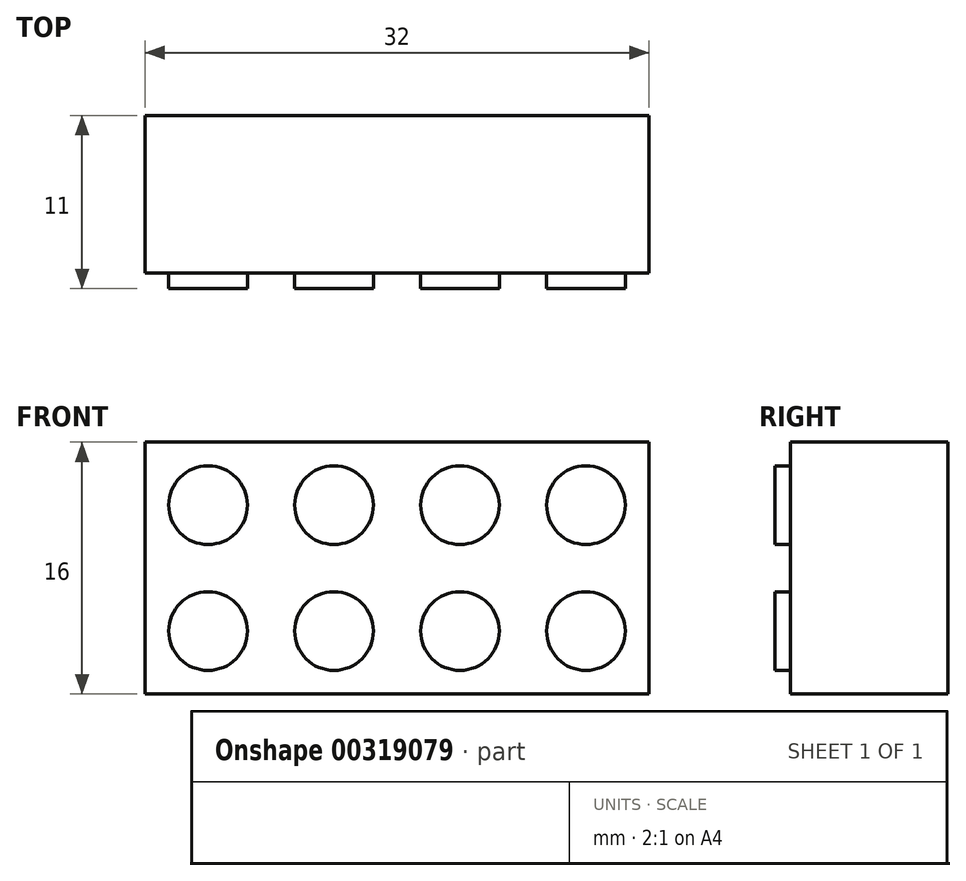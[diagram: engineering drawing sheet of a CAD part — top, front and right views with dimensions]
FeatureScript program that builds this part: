
annotation { "Feature Type Name" : "Feature", "Feature Type Description" : "" }
export const myFeature = defineFeature(function(context is Context, id is Id, definition is map)
    precondition{}
    {
        {
            var Q0;
            Q0=qCreatedBy(makeId("Front.planeOp"),FACE);
            var sketch = newSketch(context, id + "F0", { "sketchPlane" : qUnion([Q0])});
            skLineSegment(sketch, "E0.bottom", {"start": v(-16, -8) * mm, "end": v(16, -8) * mm});
            skLineSegment(sketch, "E0.top", {"start": v(-16, 8) * mm, "end": v(16, 8) * mm});
            skLineSegment(sketch, "E0.left", {"start": v(-16, -8) * mm, "end": v(-16, 8) * mm});
            skLineSegment(sketch, "E0.right", {"start": v(16, -8) * mm, "end": v(16, 8) * mm});
            skPoint(sketch, "E0.middle", {"position": v(0, 0) * mm});
            skCircle(sketch, "E1", {"center": v(-12, 4) * mm, "radius": 2.5 * mm});
            skCircle(sketch, "E2", {"center": v(-12, -4) * mm, "radius": 2.5 * mm});
            skCircle(sketch, "E3", {"center": v(-4, -4) * mm, "radius": 2.5 * mm});
            skCircle(sketch, "E4", {"center": v(4, -4) * mm, "radius": 2.5 * mm});
            skCircle(sketch, "E5", {"center": v(12, -4) * mm, "radius": 2.5 * mm});
            skCircle(sketch, "E6", {"center": v(-4, 4) * mm, "radius": 2.5 * mm});
            skCircle(sketch, "E7", {"center": v(4, 4) * mm, "radius": 2.5 * mm});
            skCircle(sketch, "E8", {"center": v(12, 4) * mm, "radius": 2.5 * mm});
            skSolve(sketch);
        }
        {
            var Q0;
            Q0=makeQuery(id+"F0.imprint","IMPRINT",FACE,{"disambiguationData":[TD([[makeQuery(id+"F0.imprint","IMPRINT",EDGE,{"derivedFrom":sQuery(id+"F0.wireOp",EDGE,"E0.bottom")}),1.0]])]});
            extrude(context, id + "F1", {"entities" : qUnion([Q0]), "oppositeDirection" : true, "depth" : 10 * mm});
        }
        {
            var Q0;
            Q0=makeQuery(id+"F1.opExtrude","CAP_FACE",FACE,{"disambiguationData":[OSD([sQuery(id+"F0.wireOp",EDGE,"E0.bottom"),sQuery(id+"F0.wireOp",EDGE,"E0.top"),sQuery(id+"F0.wireOp",EDGE,"E0.left"),sQuery(id+"F0.wireOp",EDGE,"E0.right"),sQuery(id+"F0.wireOp",EDGE,"E1"),sQuery(id+"F0.wireOp",EDGE,"E2"),sQuery(id+"F0.wireOp",EDGE,"E3"),sQuery(id+"F0.wireOp",EDGE,"E4"),sQuery(id+"F0.wireOp",EDGE,"E5"),sQuery(id+"F0.wireOp",EDGE,"E6"),sQuery(id+"F0.wireOp",EDGE,"E7"),sQuery(id+"F0.wireOp",EDGE,"E8")])],"isStart":false});
            var sketch = newSketch(context, id + "F2", { "sketchPlane" : qUnion([Q0])});
            skSolve(sketch);
        }
        {
            var Q0;
            Q0 = qSketchRegion(id + "F2", true);
            var Q1;
            Q1=makeQuery(id+"F2.imprint","IMPRINT",FACE,{"disambiguationData":[TD([[makeQuery(id+"F2.imprint","IMPRINT",EDGE,{"derivedFrom":makeQuery(id+"F1.opExtrude","CAP_EDGE",EDGE,{"disambiguationData":[OSD([sQuery(id+"F0.wireOp",EDGE,"E2")])],"isStart":false})}),-1.0]])]});
            var Q2;
            Q2=makeQuery(id+"F2.imprint","IMPRINT",FACE,{"disambiguationData":[TD([[makeQuery(id+"F2.imprint","IMPRINT",EDGE,{"derivedFrom":makeQuery(id+"F1.opExtrude","CAP_EDGE",EDGE,{"disambiguationData":[OSD([sQuery(id+"F0.wireOp",EDGE,"E1")])],"isStart":false})}),-1.0]])]});
            var Q3;
            Q3=makeQuery(id+"F2.imprint","IMPRINT",FACE,{"disambiguationData":[TD([[makeQuery(id+"F2.imprint","IMPRINT",EDGE,{"derivedFrom":makeQuery(id+"F1.opExtrude","CAP_EDGE",EDGE,{"disambiguationData":[OSD([sQuery(id+"F0.wireOp",EDGE,"E6")])],"isStart":false})}),-1.0]])]});
            var Q4;
            Q4=makeQuery(id+"F2.imprint","IMPRINT",FACE,{"disambiguationData":[TD([[makeQuery(id+"F2.imprint","IMPRINT",EDGE,{"derivedFrom":makeQuery(id+"F1.opExtrude","CAP_EDGE",EDGE,{"disambiguationData":[OSD([sQuery(id+"F0.wireOp",EDGE,"E3")])],"isStart":false})}),-1.0]])]});
            var Q5;
            Q5=makeQuery(id+"F2.imprint","IMPRINT",FACE,{"disambiguationData":[TD([[makeQuery(id+"F2.imprint","IMPRINT",EDGE,{"derivedFrom":makeQuery(id+"F1.opExtrude","CAP_EDGE",EDGE,{"disambiguationData":[OSD([sQuery(id+"F0.wireOp",EDGE,"E4")])],"isStart":false})}),-1.0]])]});
            var Q6;
            Q6=makeQuery(id+"F2.imprint","IMPRINT",FACE,{"disambiguationData":[TD([[makeQuery(id+"F2.imprint","IMPRINT",EDGE,{"derivedFrom":makeQuery(id+"F1.opExtrude","CAP_EDGE",EDGE,{"disambiguationData":[OSD([sQuery(id+"F0.wireOp",EDGE,"E7")])],"isStart":false})}),-1.0]])]});
            var Q7;
            Q7=makeQuery(id+"F2.imprint","IMPRINT",FACE,{"disambiguationData":[TD([[makeQuery(id+"F2.imprint","IMPRINT",EDGE,{"derivedFrom":makeQuery(id+"F1.opExtrude","CAP_EDGE",EDGE,{"disambiguationData":[OSD([sQuery(id+"F0.wireOp",EDGE,"E5")])],"isStart":false})}),-1.0]])]});
            var Q8;
            Q8=makeQuery(id+"F2.imprint","IMPRINT",FACE,{"disambiguationData":[TD([[makeQuery(id+"F2.imprint","IMPRINT",EDGE,{"derivedFrom":makeQuery(id+"F1.opExtrude","CAP_EDGE",EDGE,{"disambiguationData":[OSD([sQuery(id+"F0.wireOp",EDGE,"E8")])],"isStart":false})}),-1.0]])]});
            extrude(context, id + "F3", {"entities" : qUnion([Q0, Q1, Q2, Q3, Q4, Q5, Q6, Q7, Q8]), "operationType" : NewBodyOperationType.ADD, "oppositeDirection" : true, "depth" : 11 * mm});
        }
    });
